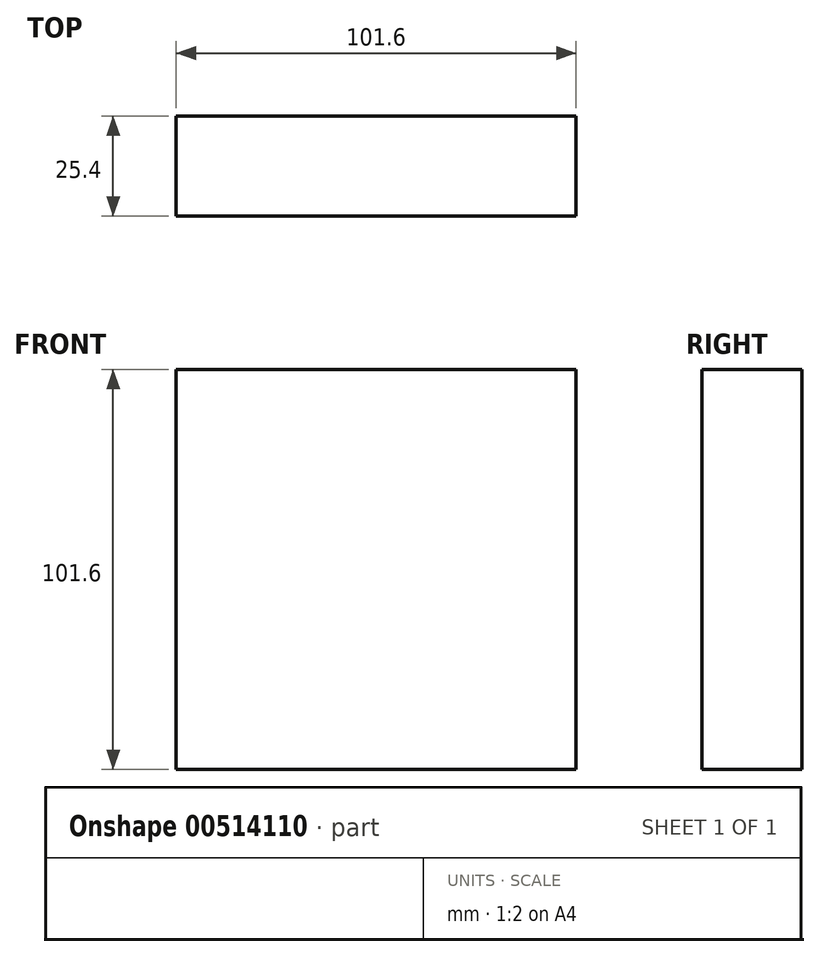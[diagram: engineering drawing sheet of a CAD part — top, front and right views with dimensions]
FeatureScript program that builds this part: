
annotation { "Feature Type Name" : "Feature", "Feature Type Description" : "" }
export const myFeature = defineFeature(function(context is Context, id is Id, definition is map)
    precondition{}
    {
        {
            var Q0;
            Q0=qCreatedBy(makeId("Front.planeOp"),FACE);
            var sketch = newSketch(context, id + "F0", { "sketchPlane" : qUnion([Q0])});
            skLineSegment(sketch, "E0.bottom", {"start": v(-49.62, 50.17) * mm, "end": v(51.98, 50.17) * mm});
            skLineSegment(sketch, "E0.top", {"start": v(-49.62, -51.43) * mm, "end": v(51.98, -51.43) * mm});
            skLineSegment(sketch, "E0.left", {"start": v(-49.62, 50.17) * mm, "end": v(-49.62, -51.43) * mm});
            skLineSegment(sketch, "E0.right", {"start": v(51.98, 50.17) * mm, "end": v(51.98, -51.43) * mm});
            skSolve(sketch);
        }
        {
            var Q0;
            Q0 = qSketchRegion(id + "F0", true);
            extrude(context, id + "F1", {"entities" : qUnion([Q0]), "depth" : 25.4 * mm});
        }
    });
